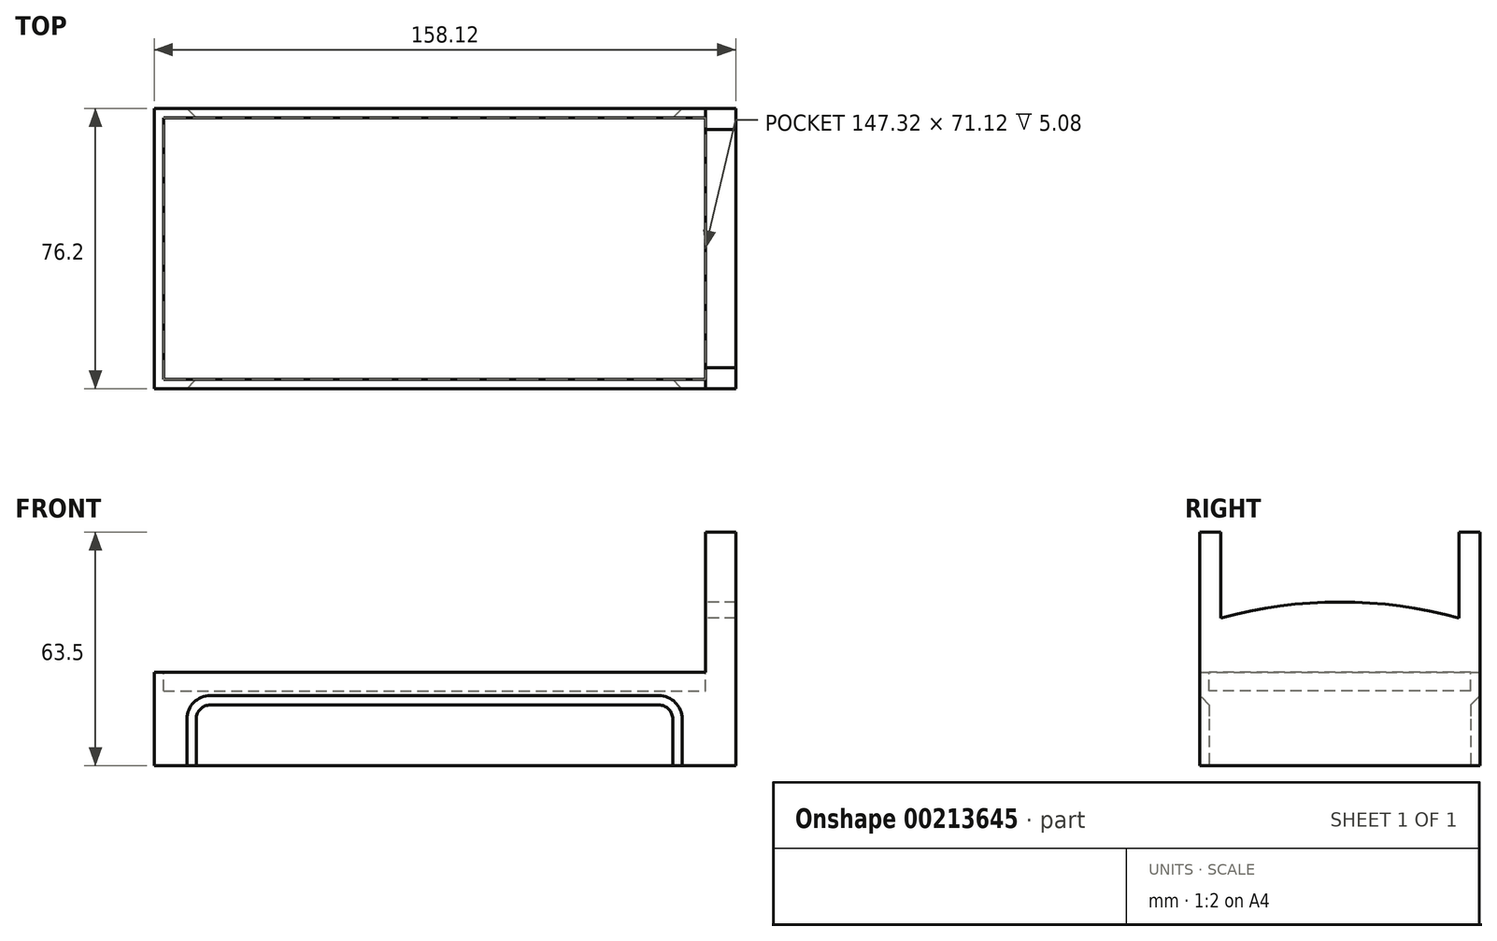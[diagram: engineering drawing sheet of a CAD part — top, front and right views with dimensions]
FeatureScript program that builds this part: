
annotation { "Feature Type Name" : "Feature", "Feature Type Description" : "" }
export const myFeature = defineFeature(function(context is Context, id is Id, definition is map)
    precondition{}
    {
        {
            var Q0;
            Q0=qCreatedBy(makeId("Top.planeOp"),FACE);
            var sketch = newSketch(context, id + "F0", { "sketchPlane" : qUnion([Q0])});
            skLineSegment(sketch, "E0.bottom", {"start": v(0, 0) * mm, "end": v(152.4, 0) * mm});
            skLineSegment(sketch, "E0.top", {"start": v(0, 76.2) * mm, "end": v(152.4, 76.2) * mm});
            skLineSegment(sketch, "E0.left", {"start": v(0, 0) * mm, "end": v(0, 76.2) * mm});
            skLineSegment(sketch, "E0.right", {"start": v(152.4, 0) * mm, "end": v(152.4, 76.2) * mm});
            skSolve(sketch);
        }
        {
            var Q0;
            Q0=makeQuery(id+"F0.imprint","IMPRINT",FACE,{"disambiguationData":[TD([[makeQuery(id+"F0.imprint","IMPRINT",EDGE,{"derivedFrom":sQuery(id+"F0.wireOp",EDGE,"E0.bottom")}),1.0]])]});
            extrude(context, id + "F1", {"entities" : qUnion([Q0]), "depth" : 25.4 * mm});
        }
        {
            var Q0;
            Q0=makeQuery(id+"F1.opExtrude","CAP_FACE",FACE,{"disambiguationData":[OSD([sQuery(id+"F0.wireOp",EDGE,"E0.bottom"),sQuery(id+"F0.wireOp",EDGE,"E0.top"),sQuery(id+"F0.wireOp",EDGE,"E0.left"),sQuery(id+"F0.wireOp",EDGE,"E0.right")])],"isStart":false});
            var sketch = newSketch(context, id + "F2", { "sketchPlane" : qUnion([Q0])});
            skLineSegment(sketch, "E1.bottom", {"start": v(2.54, 73.66) * mm, "end": v(149.86, 73.66) * mm});
            skLineSegment(sketch, "E1.top", {"start": v(2.54, 2.54) * mm, "end": v(149.86, 2.54) * mm});
            skLineSegment(sketch, "E1.left", {"start": v(2.54, 73.66) * mm, "end": v(2.54, 2.54) * mm});
            skLineSegment(sketch, "E1.right", {"start": v(149.86, 73.66) * mm, "end": v(149.86, 2.54) * mm});
            skSolve(sketch);
        }
        {
            var Q0;
            Q0=makeQuery(id+"F2.imprint","IMPRINT",FACE,{"disambiguationData":[TD([[makeQuery(id+"F2.imprint","IMPRINT",EDGE,{"derivedFrom":sQuery(id+"F2.wireOp",EDGE,"E1.bottom")}),-1.0]])]});
            extrude(context, id + "F3", {"entities" : qUnion([Q0]), "operationType" : NewBodyOperationType.REMOVE, "oppositeDirection" : true, "depth" : 5.08 * mm});
        }
        {
            var Q0;
            Q0=makeQuery(id+"F1.opExtrude","SWEPT_FACE",FACE,{"disambiguationData":[OSD([sQuery(id+"F0.wireOp",EDGE,"E0.bottom")])]});
            var sketch = newSketch(context, id + "F4", { "sketchPlane" : qUnion([Q0])});
            skLineSegment(sketch, "E2", {"start": v(8.9, 0) * mm, "end": v(8.9, 12.7) * mm});
            skLineSegment(sketch, "E3", {"start": v(15.24, 19.05) * mm, "end": v(137.16, 19.05) * mm});
            skLineSegment(sketch, "E4", {"start": v(143.51, 12.7) * mm, "end": v(143.51, 0) * mm});
            skLineSegment(sketch, "E5", {"start": v(143.51, 0) * mm, "end": v(8.9, 0) * mm});
            skPoint(sketch, "E6.visualSharp", {"position": v(8.9, 19.05) * mm});
            skArc(sketch, "E6.filletArc", {"start": v(15.24, 19.05) * mm, "mid": v(10.75, 17.2) * mm, "end": v(8.9, 12.7) * mm});
            skPoint(sketch, "E7.visualSharp", {"position": v(143.51, 19.05) * mm});
            skArc(sketch, "E7.filletArc", {"start": v(143.51, 12.7) * mm, "mid": v(141.65, 17.2) * mm, "end": v(137.16, 19.05) * mm});
            skSolve(sketch);
        }
        {
            var Q0;
            Q0=makeQuery(id+"F4.imprint","IMPRINT",FACE,{"disambiguationData":[TD([[makeQuery(id+"F4.imprint","IMPRINT",EDGE,{"derivedFrom":sQuery(id+"F4.wireOp",EDGE,"E2")}),-1.0]])]});
            extrude(context, id + "F5", {"entities" : qUnion([Q0]), "operationType" : NewBodyOperationType.REMOVE, "oppositeDirection" : true, "depth" : 2.54 * mm});
        }
        {
            var Q0;
            Q0=makeQuery(id+"F5.boolean.opBoolean","COPY",EDGE,{"derivedFrom":makeQuery(id+"F5.opExtrude","CAP_EDGE",EDGE,{"disambiguationData":[OSD([sQuery(id+"F4.wireOp",EDGE,"E3")])],"isStart":false})});
            chamfer(context, id + "F6", {"entities" : qUnion([Q0]), "width" : 2.54 * mm, "tangentPropagation" : true});
        }
        {
            var Q0;
            Q0=makeQuery(id+"F1.opExtrude","SWEPT_FACE",FACE,{"disambiguationData":[OSD([sQuery(id+"F0.wireOp",EDGE,"E0.top")])]});
            var sketch = newSketch(context, id + "F7", { "sketchPlane" : qUnion([Q0])});
            skLineSegment(sketch, "E8", {"start": v(-143.5, 0) * mm, "end": v(-143.5, 12.7) * mm});
            skLineSegment(sketch, "E9", {"start": v(-137.16, 19.05) * mm, "end": v(-15.24, 19.05) * mm});
            skLineSegment(sketch, "E10", {"start": v(-8.9, 12.7) * mm, "end": v(-8.9, 0) * mm});
            skLineSegment(sketch, "E11", {"start": v(-8.9, 0) * mm, "end": v(-143.5, 0) * mm});
            skPoint(sketch, "E12.visualSharp", {"position": v(-143.5, 19.05) * mm});
            skArc(sketch, "E12.filletArc", {"start": v(-137.16, 19.05) * mm, "mid": v(-141.65, 17.2) * mm, "end": v(-143.5, 12.7) * mm});
            skPoint(sketch, "E13.visualSharp", {"position": v(-8.9, 19.05) * mm});
            skArc(sketch, "E13.filletArc", {"start": v(-8.9, 12.7) * mm, "mid": v(-10.75, 17.2) * mm, "end": v(-15.24, 19.05) * mm});
            skSolve(sketch);
        }
        {
            var Q0;
            Q0=makeQuery(id+"F7.imprint","IMPRINT",FACE,{"disambiguationData":[TD([[makeQuery(id+"F7.imprint","IMPRINT",EDGE,{"derivedFrom":sQuery(id+"F7.wireOp",EDGE,"E8")}),-1.0]])]});
            extrude(context, id + "F8", {"entities" : qUnion([Q0]), "operationType" : NewBodyOperationType.REMOVE, "oppositeDirection" : true, "depth" : 2.54 * mm});
        }
        {
            var Q0;
            Q0=makeQuery(id+"F8.boolean.opBoolean","COPY",EDGE,{"derivedFrom":makeQuery(id+"F8.opExtrude","CAP_EDGE",EDGE,{"disambiguationData":[OSD([sQuery(id+"F7.wireOp",EDGE,"E9")])],"isStart":false})});
            chamfer(context, id + "F9", {"entities" : qUnion([Q0]), "width" : 2.54 * mm, "tangentPropagation" : true});
        }
        {
            var Q0;
            Q0=makeQuery(id+"F1.opExtrude","SWEPT_FACE",FACE,{"disambiguationData":[OSD([sQuery(id+"F0.wireOp",EDGE,"E0.right")])]});
            var sketch = newSketch(context, id + "F10", { "sketchPlane" : qUnion([Q0])});
            skLineSegment(sketch, "E14.bottom", {"start": v(0, 0) * mm, "end": v(5.72, 0) * mm});
            skLineSegment(sketch, "E14.top", {"start": v(0, 63.5) * mm, "end": v(5.71, 63.5) * mm});
            skLineSegment(sketch, "E14.left", {"start": v(0, 0) * mm, "end": v(0, 63.5) * mm});
            skLineSegment(sketch, "E14.right", {"start": v(5.72, 0) * mm, "end": v(5.71, 63.5) * mm});
            skLineSegment(sketch, "E15.bottom", {"start": v(76.2, 0) * mm, "end": v(70.49, 0) * mm});
            skLineSegment(sketch, "E15.top", {"start": v(76.2, 63.5) * mm, "end": v(70.49, 63.5) * mm});
            skLineSegment(sketch, "E15.left", {"start": v(76.2, 0) * mm, "end": v(76.2, 63.5) * mm});
            skLineSegment(sketch, "E15.right", {"start": v(70.49, 0) * mm, "end": v(70.49, 63.5) * mm});
            skArc(sketch, "E16", {"start": v(70.49, 40.15) * mm, "mid": v(38.1, 44.51) * mm, "end": v(5.71, 40.15) * mm});
            skPoint(sketch, "E16.centerSnap0", {"position": v(38.1, 0) * mm});
            skLineSegment(sketch, "E17", {"start": v(5.72, 0) * mm, "end": v(70.49, 0) * mm});
            skSolve(sketch);
        }
        {
            var Q0;
            {var subQ0=sQuery(id+"F10.wireOp",EDGE,"E16");Q0=makeQuery(id+"F10.imprint","IMPRINT",FACE,{"disambiguationData":[TD([[makeQuery(id+"F10.imprint","IMPRINT",EDGE,{"derivedFrom":subQ0}),1.0]])]});}
            var Q1;
            {var subQ0=sQuery(id+"F10.wireOp",EDGE,"E17");Q1=makeQuery(id+"F10.imprint","IMPRINT",FACE,{"disambiguationData":[TD([[makeQuery(id+"F10.imprint","IMPRINT",EDGE,{"derivedFrom":subQ0}),1.0]])]});}
            var Q2;
            {var subQ0=sQuery(id+"F10.wireOp",EDGE,"E14.bottom");Q2=makeQuery(id+"F10.imprint","IMPRINT",FACE,{"disambiguationData":[TD([[makeQuery(id+"F10.imprint","IMPRINT",EDGE,{"derivedFrom":subQ0}),1.0]])]});}
            var Q3;
            {var subQ1=sQuery(id+"F10.wireOp",EDGE,"E14.top");Q3=makeQuery(id+"F10.imprint","IMPRINT",FACE,{"disambiguationData":[TD([[makeQuery(id+"F10.imprint","IMPRINT",EDGE,{"derivedFrom":subQ1}),-1.0]])]});}
            var Q4;
            {var subQ1=sQuery(id+"F10.wireOp",EDGE,"E15.top");Q4=makeQuery(id+"F10.imprint","IMPRINT",FACE,{"disambiguationData":[TD([[makeQuery(id+"F10.imprint","IMPRINT",EDGE,{"derivedFrom":subQ1}),1.0]])]});}
            var Q5;
            {var subQ0=sQuery(id+"F10.wireOp",EDGE,"E15.bottom");Q5=makeQuery(id+"F10.imprint","IMPRINT",FACE,{"disambiguationData":[TD([[makeQuery(id+"F10.imprint","IMPRINT",EDGE,{"derivedFrom":subQ0}),1.0]])]});}
            extrude(context, id + "F11", {"entities" : qUnion([Q0, Q1, Q2, Q3, Q4, Q5]), "operationType" : NewBodyOperationType.ADD, "depth" : 5.7 * mm, "hasSecondDirection" : true, "secondDirectionOppositeDirection" : true, "secondDirectionDepth" : 2.54 * mm});
        }
    });
